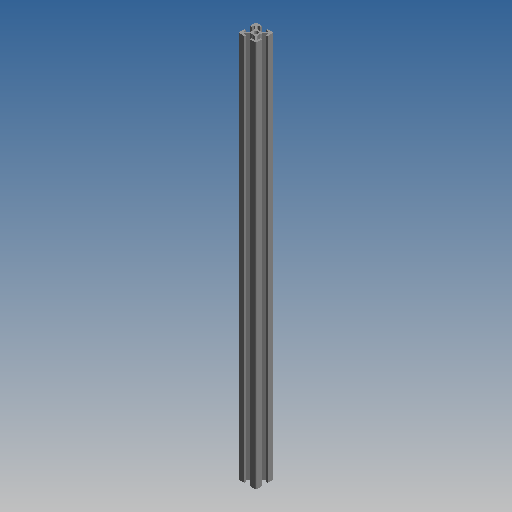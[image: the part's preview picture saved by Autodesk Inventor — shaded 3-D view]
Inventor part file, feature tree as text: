
AUTODESK INVENTOR PART (.ipt)
format: ipt  version: 2020 (Build 240168000, 168)  size: 209,408 bytes
history: native  units: mm (DEFAULTED — no unit token found)
features: other x7, sketch x2, extrude x1, hole x1
ambient origin geometry x8: Origin, YZ Plane, XZ Plane, XY Plane, X Axis, Y Axis, Z Axis, Center Point
bodies: Solid1 (feature_tree)
feature tree (11):
  extrude  "Extrusion1"  TaperAngle=0.0deg  [1 undecoded]
  hole  "Hole1"  [1 undecoded]
  other  "C1_XY"
  other  "C1_YZ"
  other  "C1_ZX"
  other  "C1_X"
  other  "C1_Y"
  other  "C1_Z"
  other  "C1_Center"
  sketch  "Sketch_75"  dims[d2=4.2mm d3=6.0mm d4=4.0mm d5=2.0mm d6=90.0deg d7=437.0mm d8=0.0mm d9=0.0mm]
  sketch  "Sketch2"  dims[d0=437.0mm d1=0.0mm]
note: 2 required parameter values undecoded (feature->parameter linkage not recoverable at this tier; creation-order binding heuristic only, values carry confidence <= 0.55)
